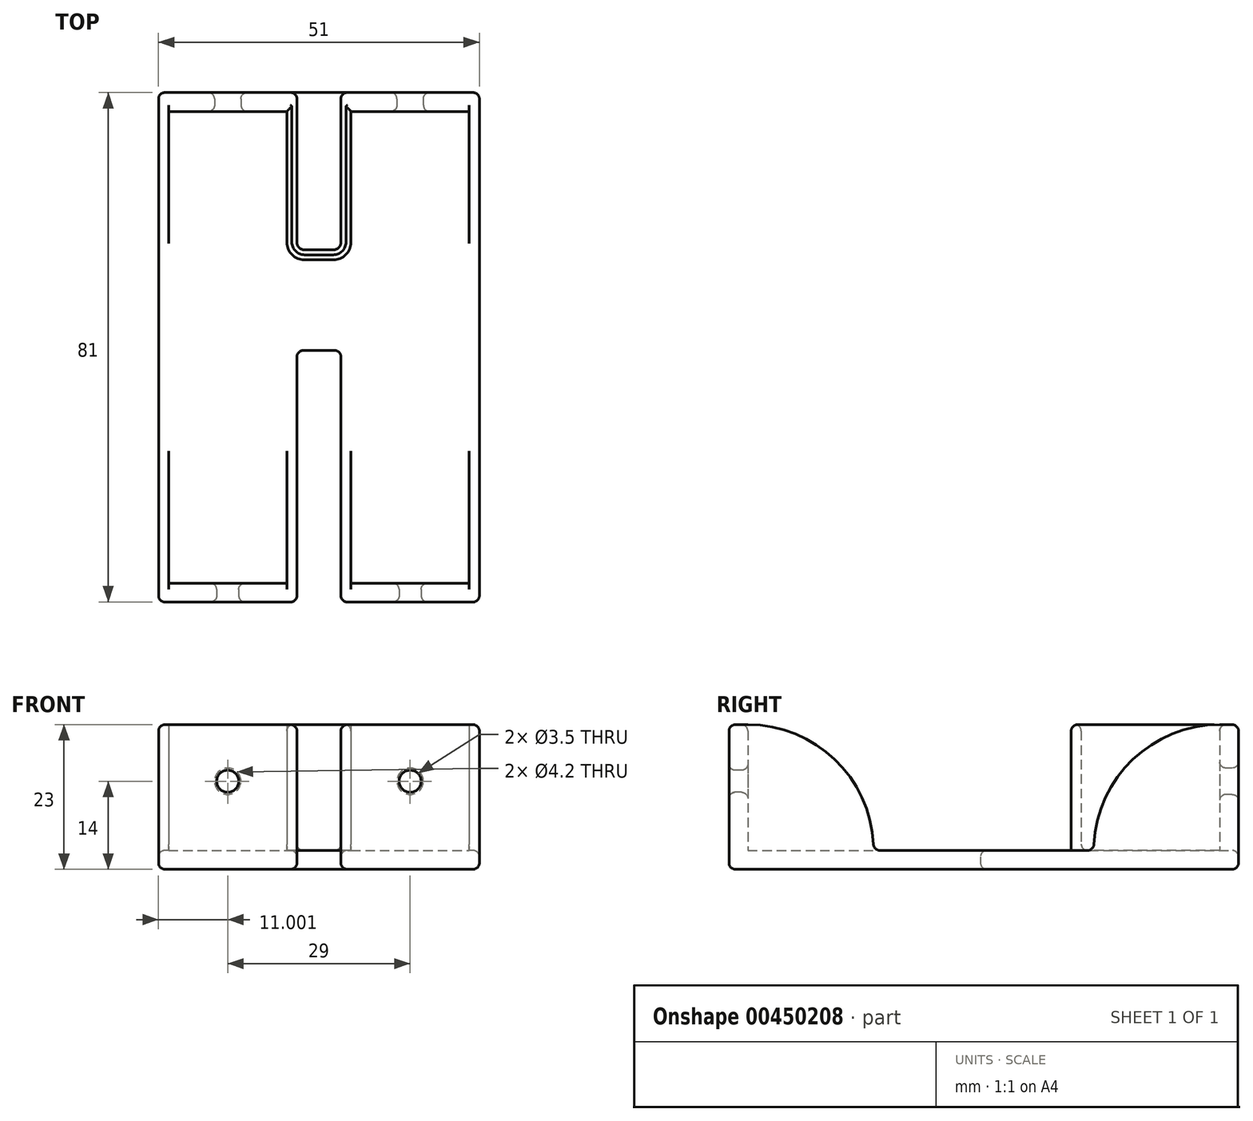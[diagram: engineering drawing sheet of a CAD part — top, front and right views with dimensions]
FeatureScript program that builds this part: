
annotation { "Feature Type Name" : "Feature", "Feature Type Description" : "" }
export const myFeature = defineFeature(function(context is Context, id is Id, definition is map)
    precondition{}
    {
        {
            var Q0;
            Q0=qCreatedBy(makeId("Top.planeOp"),FACE);
            var sketch = newSketch(context, id + "F0", { "sketchPlane" : qUnion([Q0])});
            skLineSegment(sketch, "E0", {"start": v(0.78, 0) * mm, "end": v(22.78, 0) * mm});
            skLineSegment(sketch, "E1", {"start": v(0.78, 0) * mm, "end": v(0.78, 3) * mm});
            skLineSegment(sketch, "E2", {"start": v(0.78, 3) * mm, "end": v(0.78, 78) * mm});
            skLineSegment(sketch, "E3", {"start": v(0.78, 78) * mm, "end": v(0.78, 81) * mm});
            skLineSegment(sketch, "E4", {"start": v(0.78, 81) * mm, "end": v(22.78, 81) * mm});
            skLineSegment(sketch, "E5", {"start": v(22.78, 81) * mm, "end": v(29.78, 81) * mm});
            skLineSegment(sketch, "E6", {"start": v(29.78, 81) * mm, "end": v(51.78, 81) * mm});
            skLineSegment(sketch, "E7", {"start": v(51.78, 81) * mm, "end": v(51.78, 0) * mm});
            skLineSegment(sketch, "E8", {"start": v(51.78, 0) * mm, "end": v(29.78, 0) * mm});
            skLineSegment(sketch, "E9", {"start": v(29.78, 0) * mm, "end": v(29.78, 40) * mm});
            skLineSegment(sketch, "E10", {"start": v(22.78, 0) * mm, "end": v(22.78, 40) * mm});
            skLineSegment(sketch, "E11", {"start": v(22.78, 40) * mm, "end": v(29.78, 40) * mm});
            skLineSegment(sketch, "E12", {"start": v(2.38, 78) * mm, "end": v(21.18, 78) * mm});
            skLineSegment(sketch, "E13", {"start": v(22.78, 78) * mm, "end": v(22.78, 81) * mm});
            skLineSegment(sketch, "E14", {"start": v(29.78, 81) * mm, "end": v(29.78, 78) * mm});
            skLineSegment(sketch, "E15", {"start": v(31.38, 78) * mm, "end": v(50.18, 78) * mm});
            skLineSegment(sketch, "E16", {"start": v(31.38, 3) * mm, "end": v(50.18, 3) * mm});
            skLineSegment(sketch, "E17", {"start": v(22.78, 78) * mm, "end": v(22.78, 57.2) * mm});
            skLineSegment(sketch, "E18", {"start": v(23.98, 56) * mm, "end": v(28.58, 56) * mm});
            skLineSegment(sketch, "E19", {"start": v(29.78, 57.2) * mm, "end": v(29.78, 78) * mm});
            skLineSegment(sketch, "E20.0", {"start": v(21.18, 78) * mm, "end": v(21.18, 57.2) * mm});
            skLineSegment(sketch, "E21.0", {"start": v(23.98, 54.4) * mm, "end": v(28.58, 54.4) * mm});
            skLineSegment(sketch, "E22.0", {"start": v(31.38, 57.2) * mm, "end": v(31.38, 78) * mm});
            skLineSegment(sketch, "E23", {"start": v(2.38, 78) * mm, "end": v(2.38, 58) * mm});
            skLineSegment(sketch, "E24", {"start": v(2.38, 58) * mm, "end": v(0.78, 58) * mm});
            skLineSegment(sketch, "E25", {"start": v(50.18, 78) * mm, "end": v(50.18, 58) * mm});
            skLineSegment(sketch, "E26", {"start": v(50.18, 58) * mm, "end": v(51.78, 58) * mm});
            skLineSegment(sketch, "E27", {"start": v(2.38, 3) * mm, "end": v(2.38, 23) * mm});
            skLineSegment(sketch, "E28", {"start": v(2.38, 23) * mm, "end": v(0.78, 23) * mm});
            skLineSegment(sketch, "E29", {"start": v(21.18, 3) * mm, "end": v(21.18, 23) * mm});
            skLineSegment(sketch, "E30", {"start": v(21.18, 23) * mm, "end": v(22.78, 23) * mm});
            skLineSegment(sketch, "E31", {"start": v(31.38, 3) * mm, "end": v(31.38, 23) * mm});
            skLineSegment(sketch, "E32", {"start": v(31.38, 23) * mm, "end": v(29.78, 23) * mm});
            skLineSegment(sketch, "E33", {"start": v(50.18, 3) * mm, "end": v(50.18, 23) * mm});
            skLineSegment(sketch, "E34", {"start": v(50.18, 23) * mm, "end": v(51.78, 23) * mm});
            skPoint(sketch, "E35.start.orphan", {"position": v(51.78, 3) * mm});
            skPoint(sketch, "E36.orphan", {"position": v(29.78, 3) * mm});
            skPoint(sketch, "E37.orphan", {"position": v(22.78, 3) * mm});
            skPoint(sketch, "E38.orphan", {"position": v(51.78, 78) * mm});
            skPoint(sketch, "E39.visualSharp", {"position": v(22.78, 56) * mm});
            skArc(sketch, "E39.filletArc", {"start": v(22.78, 57.2) * mm, "mid": v(23.13, 56.35) * mm, "end": v(23.98, 56) * mm});
            skPoint(sketch, "E40.visualSharp", {"position": v(29.78, 56) * mm});
            skArc(sketch, "E40.filletArc", {"start": v(28.58, 56) * mm, "mid": v(29.43, 56.35) * mm, "end": v(29.78, 57.2) * mm});
            skArc(sketch, "E41", {"start": v(23.98, 54.4) * mm, "mid": v(22, 55.22) * mm, "end": v(21.18, 57.2) * mm});
            skArc(sketch, "E42", {"start": v(28.58, 54.4) * mm, "mid": v(30.56, 55.22) * mm, "end": v(31.38, 57.2) * mm});
            skLineSegment(sketch, "E43", {"start": v(2.38, 3) * mm, "end": v(21.18, 3) * mm});
            skSolve(sketch);
        }
        {
            var Q0;
            {var subQ2=sQuery(id+"F0.wireOp",EDGE,"E3");Q0=makeQuery(id+"F0.imprint","IMPRINT",FACE,{"disambiguationData":[TD([[makeQuery(id+"F0.imprint","IMPRINT",EDGE,{"derivedFrom":subQ2}),-1.0]])]});}
            var Q1;
            {var subQ4=sQuery(id+"F0.wireOp",EDGE,"E0");Q1=makeQuery(id+"F0.imprint","IMPRINT",FACE,{"disambiguationData":[TD([[makeQuery(id+"F0.imprint","IMPRINT",EDGE,{"derivedFrom":subQ4}),1.0]])]});}
            var Q2;
            {var subQ1=sQuery(id+"F0.wireOp",EDGE,"E8");Q2=makeQuery(id+"F0.imprint","IMPRINT",FACE,{"disambiguationData":[TD([[makeQuery(id+"F0.imprint","IMPRINT",EDGE,{"derivedFrom":subQ1}),-1.0]])]});}
            extrude(context, id + "F1", {"entities" : qUnion([Q0, Q1, Q2]), "depth" : 23 * mm});
        }
        {
            var Q0;
            {var subQ5=sQuery(id+"F0.wireOp",EDGE,"E11");Q0=makeQuery(id+"F0.imprint","IMPRINT",FACE,{"disambiguationData":[TD([[makeQuery(id+"F0.imprint","IMPRINT",EDGE,{"derivedFrom":subQ5}),1.0]])]});}
            var Q1;
            Q1=makeQuery(id+"F0.imprint","IMPRINT",FACE,{"disambiguationData":[TD([[makeQuery(id+"F0.imprint","IMPRINT",EDGE,{"derivedFrom":sQuery(id+"F0.wireOp",EDGE,"E5")}),-1.0]])]});
            extrude(context, id + "F2", {"entities" : qUnion([Q0, Q1]), "operationType" : NewBodyOperationType.ADD, "depth" : 3 * mm});
        }
        {
            var Q0;
            Q0=makeQuery(id+"F1.opExtrude","CAP_EDGE",EDGE,{"disambiguationData":[OSD([sQuery(id+"F0.wireOp",EDGE,"E24")])],"isStart":false});
            var Q1;
            Q1=makeQuery(id+"F1.opExtrude","CAP_EDGE",EDGE,{"disambiguationData":[OSD([sQuery(id+"F0.wireOp",EDGE,"E26")])],"isStart":false});
            var Q2;
            Q2=makeQuery(id+"F1.opExtrude","CAP_EDGE",EDGE,{"disambiguationData":[OSD([sQuery(id+"F0.wireOp",EDGE,"E34")])],"isStart":false});
            var Q3;
            Q3=makeQuery(id+"F1.opExtrude","CAP_EDGE",EDGE,{"disambiguationData":[OSD([sQuery(id+"F0.wireOp",EDGE,"E32")])],"isStart":false});
            var Q4;
            Q4=makeQuery(id+"F1.opExtrude","CAP_EDGE",EDGE,{"disambiguationData":[OSD([sQuery(id+"F0.wireOp",EDGE,"E30")])],"isStart":false});
            var Q5;
            Q5=makeQuery(id+"F1.opExtrude","CAP_EDGE",EDGE,{"disambiguationData":[OSD([sQuery(id+"F0.wireOp",EDGE,"E28")])],"isStart":false});
            fillet(context, id + "F3", {"entities" : qUnion([Q0, Q1, Q2, Q3, Q4, Q5]), "radius" : 20 * mm, "tangentPropagation" : true, "allowEdgeOverflow" : false});
        }
        {
            var Q0;
            Q0=makeQuery(id+"F1.opExtrude","SWEPT_FACE",FACE,{"disambiguationData":[OSD([sQuery(id+"F0.wireOp",EDGE,"E0")])]});
            var sketch = newSketch(context, id + "F4", { "sketchPlane" : qUnion([Q0])});
            skCircle(sketch, "E44", {"center": v(11.78, 14) * mm, "radius": 1.75 * mm});
            skLineSegment(sketch, "E45.0.0", {"start": v(0.78, 0) * mm, "end": v(22.78, 0) * mm});
            skLineSegment(sketch, "E45.0.1", {"start": v(22.78, 0) * mm, "end": v(22.78, 23) * mm});
            skLineSegment(sketch, "E45.0.2", {"start": v(22.78, 23) * mm, "end": v(0.78, 23) * mm});
            skLineSegment(sketch, "E45.0.3", {"start": v(0.78, 23) * mm, "end": v(0.78, 0) * mm});
            skSolve(sketch);
        }
        {
            var Q0;
            Q0=makeQuery(id+"F1.opExtrude","SWEPT_FACE",FACE,{"disambiguationData":[OSD([sQuery(id+"F0.wireOp",EDGE,"E8")])]});
            var sketch = newSketch(context, id + "F5", { "sketchPlane" : qUnion([Q0])});
            skCircle(sketch, "E46", {"center": v(40.78, 14) * mm, "radius": 1.75 * mm});
            skSolve(sketch);
        }
        {
            var Q0;
            Q0=makeQuery(id+"F2.boolean.opBoolean","MERGE",FACE,{"derivedFrom":[makeQuery(id+"F1.opExtrude","SWEPT_FACE",FACE,{"disambiguationData":[OSD([sQuery(id+"F0.wireOp",EDGE,"E4")])]}),makeQuery(id+"F1.opExtrude","SWEPT_FACE",FACE,{"disambiguationData":[OSD([sQuery(id+"F0.wireOp",EDGE,"E6")])]}),makeQuery(id+"F2.opExtrude","SWEPT_FACE",FACE,{"disambiguationData":[OSD([sQuery(id+"F0.wireOp",EDGE,"E5")])]})]});
            var sketch = newSketch(context, id + "F6", { "sketchPlane" : qUnion([Q0])});
            skCircle(sketch, "E47", {"center": v(-40.78, 14) * mm, "radius": 2.1 * mm});
            skCircle(sketch, "E48", {"center": v(-11.78, 14) * mm, "radius": 2.1 * mm});
            skLineSegment(sketch, "E49.0.0", {"start": v(-51.78, 0) * mm, "end": v(-0.78, 0) * mm});
            skLineSegment(sketch, "E49.0.1", {"start": v(-0.78, 0) * mm, "end": v(-0.78, 23) * mm});
            skLineSegment(sketch, "E49.0.2", {"start": v(-0.78, 23) * mm, "end": v(-22.78, 23) * mm});
            skLineSegment(sketch, "E49.0.3", {"start": v(-22.78, 23) * mm, "end": v(-22.78, 3) * mm});
            skLineSegment(sketch, "E49.0.4", {"start": v(-22.78, 3) * mm, "end": v(-29.78, 3) * mm});
            skLineSegment(sketch, "E49.0.5", {"start": v(-29.78, 3) * mm, "end": v(-29.78, 23) * mm});
            skLineSegment(sketch, "E49.0.6", {"start": v(-29.78, 23) * mm, "end": v(-51.78, 23) * mm});
            skLineSegment(sketch, "E49.0.7", {"start": v(-51.78, 23) * mm, "end": v(-51.78, 0) * mm});
            skSolve(sketch);
        }
        {
            var Q0;
            Q0=makeQuery(id+"F6.imprint","IMPRINT",FACE,{"disambiguationData":[TD([[makeQuery(id+"F6.imprint","IMPRINT",EDGE,{"derivedFrom":sQuery(id+"F6.wireOp",EDGE,"E47")}),1.0]])]});
            var Q1;
            Q1=makeQuery(id+"F6.imprint","IMPRINT",FACE,{"disambiguationData":[TD([[makeQuery(id+"F6.imprint","IMPRINT",EDGE,{"derivedFrom":sQuery(id+"F6.wireOp",EDGE,"E48")}),1.0]])]});
            var Q2;
            Q2=makeQuery(id+"F5.imprint","IMPRINT",FACE,{"disambiguationData":[TD([[makeQuery(id+"F5.imprint","IMPRINT",EDGE,{"derivedFrom":sQuery(id+"F5.wireOp",EDGE,"E46")}),1.0]])]});
            var Q3;
            Q3=makeQuery(id+"F4.imprint","IMPRINT",FACE,{"disambiguationData":[TD([[makeQuery(id+"F4.imprint","IMPRINT",EDGE,{"derivedFrom":sQuery(id+"F4.wireOp",EDGE,"E44")}),1.0]])]});
            extrude(context, id + "F7", {"entities" : qUnion([Q0, Q1, Q2, Q3]), "operationType" : NewBodyOperationType.REMOVE, "endBound" : BoundingType.SYMMETRIC, "depth" : 25 * mm});
        }
        {
            var Q0;
            Q0=makeQuery(id+"F1.opExtrude","CAP_FACE",FACE,{"disambiguationData":[OSD([sQuery(id+"F0.wireOp",EDGE,"E2"),sQuery(id+"F0.wireOp",EDGE,"E3"),sQuery(id+"F0.wireOp",EDGE,"E4"),sQuery(id+"F0.wireOp",EDGE,"E6"),sQuery(id+"F0.wireOp",EDGE,"E7"),sQuery(id+"F0.wireOp",EDGE,"E12"),sQuery(id+"F0.wireOp",EDGE,"E13"),sQuery(id+"F0.wireOp",EDGE,"E14"),sQuery(id+"F0.wireOp",EDGE,"E15"),sQuery(id+"F0.wireOp",EDGE,"E17"),sQuery(id+"F0.wireOp",EDGE,"E18"),sQuery(id+"F0.wireOp",EDGE,"E19"),sQuery(id+"F0.wireOp",EDGE,"E20.0"),sQuery(id+"F0.wireOp",EDGE,"E21.0"),sQuery(id+"F0.wireOp",EDGE,"E22.0"),sQuery(id+"F0.wireOp",EDGE,"E23"),sQuery(id+"F0.wireOp",EDGE,"E24"),sQuery(id+"F0.wireOp",EDGE,"E25"),sQuery(id+"F0.wireOp",EDGE,"E26"),sQuery(id+"F0.wireOp",EDGE,"E39.filletArc"),sQuery(id+"F0.wireOp",EDGE,"E40.filletArc"),sQuery(id+"F0.wireOp",EDGE,"E41"),sQuery(id+"F0.wireOp",EDGE,"E42")])],"isStart":false});
            var Q1;
            Q1=makeQuery(id+"F1.opExtrude","CAP_FACE",FACE,{"disambiguationData":[OSD([sQuery(id+"F0.wireOp",EDGE,"E0"),sQuery(id+"F0.wireOp",EDGE,"E1"),sQuery(id+"F0.wireOp",EDGE,"E2"),sQuery(id+"F0.wireOp",EDGE,"E10"),sQuery(id+"F0.wireOp",EDGE,"E27"),sQuery(id+"F0.wireOp",EDGE,"E28"),sQuery(id+"F0.wireOp",EDGE,"E29"),sQuery(id+"F0.wireOp",EDGE,"E30"),sQuery(id+"F0.wireOp",EDGE,"E43")])],"isStart":false});
            var Q2;
            Q2=makeQuery(id+"F1.opExtrude","CAP_FACE",FACE,{"disambiguationData":[OSD([sQuery(id+"F0.wireOp",EDGE,"E7"),sQuery(id+"F0.wireOp",EDGE,"E8"),sQuery(id+"F0.wireOp",EDGE,"E9"),sQuery(id+"F0.wireOp",EDGE,"E16"),sQuery(id+"F0.wireOp",EDGE,"E31"),sQuery(id+"F0.wireOp",EDGE,"E32"),sQuery(id+"F0.wireOp",EDGE,"E33"),sQuery(id+"F0.wireOp",EDGE,"E34")])],"isStart":false});
            var Q3;
            Q3=makeQuery(id+"F2.opExtrude","CAP_EDGE",EDGE,{"disambiguationData":[OSD([sQuery(id+"F0.wireOp",EDGE,"E10")])],"isStart":false});
            var Q4;
            Q4=makeQuery(id+"F2.opExtrude","CAP_EDGE",EDGE,{"disambiguationData":[OSD([sQuery(id+"F0.wireOp",EDGE,"E9")])],"isStart":false});
            var Q5;
            Q5=makeQuery(id+"F2.opExtrude","CAP_EDGE",EDGE,{"disambiguationData":[OSD([sQuery(id+"F0.wireOp",EDGE,"E11")])],"isStart":false});
            var Q6;
            Q6=makeQuery(id+"F2.opExtrude","CAP_EDGE",EDGE,{"disambiguationData":[OSD([sQuery(id+"F0.wireOp",EDGE,"E7")])],"isStart":false});
            var Q7;
            Q7=makeQuery(id+"F2.opExtrude","CAP_EDGE",EDGE,{"disambiguationData":[OSD([sQuery(id+"F0.wireOp",EDGE,"E2")])],"isStart":false});
            var Q8;
            {var subQ0=sQuery(id+"F0.wireOp",EDGE,"E2");Q8=makeQuery(id+"F2.boolean.opBoolean","MERGE",FACE,{"derivedFrom":[makeQuery(id+"F1.opExtrude","SWEPT_FACE",FACE,{"disambiguationData":[OSD([sQuery(id+"F0.wireOp",EDGE,"E1"),subQ0])]}),makeQuery(id+"F1.opExtrude","SWEPT_FACE",FACE,{"disambiguationData":[OSD([subQ0,sQuery(id+"F0.wireOp",EDGE,"E3")])]}),makeQuery(id+"F2.opExtrude","SWEPT_FACE",FACE,{"disambiguationData":[OSD([subQ0])]})]});}
            var Q9;
            Q9=makeQuery(id+"F2.boolean.opBoolean","MERGE",FACE,{"derivedFrom":[makeQuery(id+"F1.opExtrude","SWEPT_FACE",FACE,{"disambiguationData":[OSD([sQuery(id+"F0.wireOp",EDGE,"E4")])]}),makeQuery(id+"F1.opExtrude","SWEPT_FACE",FACE,{"disambiguationData":[OSD([sQuery(id+"F0.wireOp",EDGE,"E6")])]}),makeQuery(id+"F2.opExtrude","SWEPT_FACE",FACE,{"disambiguationData":[OSD([sQuery(id+"F0.wireOp",EDGE,"E5")])]})]});
            var Q10;
            Q10=makeQuery(id+"F7.boolean.opBoolean","INTERSECT",EDGE,{"derivedFrom":[makeQuery(id+"F1.opExtrude","SWEPT_FACE",FACE,{"disambiguationData":[OSD([sQuery(id+"F0.wireOp",EDGE,"E12")])]}),makeQuery(id+"F7.opExtrude","SWEPT_FACE",FACE,{"disambiguationData":[OSD([sQuery(id+"F6.wireOp",EDGE,"E48")])]})]});
            var Q11;
            Q11=makeQuery(id+"F7.boolean.opBoolean","INTERSECT",EDGE,{"derivedFrom":[makeQuery(id+"F1.opExtrude","SWEPT_FACE",FACE,{"disambiguationData":[OSD([sQuery(id+"F0.wireOp",EDGE,"E15")])]}),makeQuery(id+"F7.opExtrude","SWEPT_FACE",FACE,{"disambiguationData":[OSD([sQuery(id+"F6.wireOp",EDGE,"E47")])]})]});
            var Q12;
            Q12=makeQuery(id+"F1.opExtrude","SWEPT_FACE",FACE,{"disambiguationData":[OSD([sQuery(id+"F0.wireOp",EDGE,"E8")])]});
            var Q13;
            Q13=makeQuery(id+"F1.opExtrude","SWEPT_FACE",FACE,{"disambiguationData":[OSD([sQuery(id+"F0.wireOp",EDGE,"E0")])]});
            var Q14;
            Q14=makeQuery(id+"F7.boolean.opBoolean","INTERSECT",EDGE,{"derivedFrom":[makeQuery(id+"F1.opExtrude","SWEPT_FACE",FACE,{"disambiguationData":[OSD([sQuery(id+"F0.wireOp",EDGE,"E43")])]}),makeQuery(id+"F7.opExtrude","SWEPT_FACE",FACE,{"disambiguationData":[OSD([sQuery(id+"F4.wireOp",EDGE,"E44")])]})]});
            var Q15;
            Q15=makeQuery(id+"F7.boolean.opBoolean","INTERSECT",EDGE,{"derivedFrom":[makeQuery(id+"F1.opExtrude","SWEPT_FACE",FACE,{"disambiguationData":[OSD([sQuery(id+"F0.wireOp",EDGE,"E16")])]}),makeQuery(id+"F7.opExtrude","SWEPT_FACE",FACE,{"disambiguationData":[OSD([sQuery(id+"F5.wireOp",EDGE,"E46")])]})]});
            var Q16;
            {var subQ0=sQuery(id+"F0.wireOp",EDGE,"E40.filletArc");var subQ1=sQuery(id+"F0.wireOp",EDGE,"E39.filletArc");var subQ2=sQuery(id+"F0.wireOp",EDGE,"E19");var subQ3=sQuery(id+"F0.wireOp",EDGE,"E18");var subQ4=sQuery(id+"F0.wireOp",EDGE,"E17");var subQ5=sQuery(id+"F0.wireOp",EDGE,"E14");var subQ6=sQuery(id+"F0.wireOp",EDGE,"E13");var subQ7=sQuery(id+"F0.wireOp",EDGE,"E43");var subQ8=sQuery(id+"F0.wireOp",EDGE,"E42");var subQ9=sQuery(id+"F0.wireOp",EDGE,"E41");var subQ10=sQuery(id+"F0.wireOp",EDGE,"E34");var subQ11=sQuery(id+"F0.wireOp",EDGE,"E33");var subQ12=sQuery(id+"F0.wireOp",EDGE,"E32");var subQ13=sQuery(id+"F0.wireOp",EDGE,"E31");var subQ14=sQuery(id+"F0.wireOp",EDGE,"E30");var subQ15=sQuery(id+"F0.wireOp",EDGE,"E29");var subQ16=sQuery(id+"F0.wireOp",EDGE,"E28");var subQ17=sQuery(id+"F0.wireOp",EDGE,"E27");var subQ18=sQuery(id+"F0.wireOp",EDGE,"E26");var subQ19=sQuery(id+"F0.wireOp",EDGE,"E25");var subQ20=sQuery(id+"F0.wireOp",EDGE,"E24");var subQ21=sQuery(id+"F0.wireOp",EDGE,"E23");var subQ22=sQuery(id+"F0.wireOp",EDGE,"E22.0");var subQ23=sQuery(id+"F0.wireOp",EDGE,"E21.0");var subQ24=sQuery(id+"F0.wireOp",EDGE,"E20.0");var subQ25=sQuery(id+"F0.wireOp",EDGE,"E16");var subQ26=sQuery(id+"F0.wireOp",EDGE,"E15");var subQ27=sQuery(id+"F0.wireOp",EDGE,"E12");var subQ28=sQuery(id+"F0.wireOp",EDGE,"E10");var subQ29=sQuery(id+"F0.wireOp",EDGE,"E9");var subQ30=sQuery(id+"F0.wireOp",EDGE,"E7");var subQ31=sQuery(id+"F0.wireOp",EDGE,"E2");Q16=makeQuery(id+"F2.boolean.opBoolean","MERGE",FACE,{"derivedFrom":[makeQuery(id+"F1.opExtrude","CAP_FACE",FACE,{"disambiguationData":[OSD([sQuery(id+"F0.wireOp",EDGE,"E0"),sQuery(id+"F0.wireOp",EDGE,"E1"),subQ31,subQ28,subQ17,subQ16,subQ15,subQ14,subQ7])],"isStart":true}),makeQuery(id+"F1.opExtrude","CAP_FACE",FACE,{"disambiguationData":[OSD([subQ31,sQuery(id+"F0.wireOp",EDGE,"E3"),sQuery(id+"F0.wireOp",EDGE,"E4"),sQuery(id+"F0.wireOp",EDGE,"E6"),subQ30,subQ27,subQ6,subQ5,subQ26,subQ4,subQ3,subQ2,subQ24,subQ23,subQ22,subQ21,subQ20,subQ19,subQ18,subQ1,subQ0,subQ9,subQ8])],"isStart":true}),makeQuery(id+"F1.opExtrude","CAP_FACE",FACE,{"disambiguationData":[OSD([subQ30,sQuery(id+"F0.wireOp",EDGE,"E8"),subQ29,subQ25,subQ13,subQ12,subQ11,subQ10])],"isStart":true}),makeQuery(id+"F2.opExtrude","CAP_FACE",FACE,{"disambiguationData":[OSD([subQ31,subQ30,subQ29,subQ28,sQuery(id+"F0.wireOp",EDGE,"E11"),subQ27,subQ26,subQ25,subQ24,subQ23,subQ22,subQ21,subQ20,subQ19,subQ18,subQ17,subQ16,subQ15,subQ14,subQ13,subQ12,subQ11,subQ10,subQ9,subQ8,subQ7])],"isStart":true}),makeQuery(id+"F2.opExtrude","CAP_FACE",FACE,{"disambiguationData":[OSD([sQuery(id+"F0.wireOp",EDGE,"E5"),subQ6,subQ5,subQ4,subQ3,subQ2,subQ1,subQ0])],"isStart":true})]});}
            var Q17;
            Q17=makeQuery(id+"F2.opExtrude","CAP_EDGE",EDGE,{"disambiguationData":[OSD([sQuery(id+"F0.wireOp",EDGE,"E21.0")])],"isStart":false});
            var Q18;
            Q18=makeQuery(id+"F2.opExtrude","CAP_EDGE",EDGE,{"disambiguationData":[OSD([sQuery(id+"F0.wireOp",EDGE,"E42")])],"isStart":false});
            var Q19;
            Q19=makeQuery(id+"F2.opExtrude","CAP_EDGE",EDGE,{"disambiguationData":[OSD([sQuery(id+"F0.wireOp",EDGE,"E23")])],"isStart":false});
            var Q20;
            Q20=makeQuery(id+"F2.opExtrude","CAP_EDGE",EDGE,{"disambiguationData":[OSD([sQuery(id+"F0.wireOp",EDGE,"E12")])],"isStart":false});
            var Q21;
            {var subQ0=sQuery(id+"F0.wireOp",EDGE,"E24");Q21=makeQuery(id+"F3.opFillet","BLEND_EDGE",EDGE,{"blendedFrom":[makeQuery(id+"F1.opExtrude","CAP_EDGE",EDGE,{"disambiguationData":[OSD([subQ0])],"isStart":false}),makeQuery(id+"F2.opExtrude","CAP_FACE",FACE,{"disambiguationData":[OSD([sQuery(id+"F0.wireOp",EDGE,"E2"),sQuery(id+"F0.wireOp",EDGE,"E7"),sQuery(id+"F0.wireOp",EDGE,"E9"),sQuery(id+"F0.wireOp",EDGE,"E10"),sQuery(id+"F0.wireOp",EDGE,"E11"),sQuery(id+"F0.wireOp",EDGE,"E12"),sQuery(id+"F0.wireOp",EDGE,"E15"),sQuery(id+"F0.wireOp",EDGE,"E16"),sQuery(id+"F0.wireOp",EDGE,"E20.0"),sQuery(id+"F0.wireOp",EDGE,"E21.0"),sQuery(id+"F0.wireOp",EDGE,"E22.0"),sQuery(id+"F0.wireOp",EDGE,"E23"),subQ0,sQuery(id+"F0.wireOp",EDGE,"E25"),sQuery(id+"F0.wireOp",EDGE,"E26"),sQuery(id+"F0.wireOp",EDGE,"E27"),sQuery(id+"F0.wireOp",EDGE,"E28"),sQuery(id+"F0.wireOp",EDGE,"E29"),sQuery(id+"F0.wireOp",EDGE,"E30"),sQuery(id+"F0.wireOp",EDGE,"E31"),sQuery(id+"F0.wireOp",EDGE,"E32"),sQuery(id+"F0.wireOp",EDGE,"E33"),sQuery(id+"F0.wireOp",EDGE,"E34"),sQuery(id+"F0.wireOp",EDGE,"E41"),sQuery(id+"F0.wireOp",EDGE,"E42"),sQuery(id+"F0.wireOp",EDGE,"E43")])],"isStart":false})],"blendedInto":[makeQuery(id+"F2.opExtrude","CAP_FACE",FACE,{"disambiguationData":[OSD([sQuery(id+"F0.wireOp",EDGE,"E2"),sQuery(id+"F0.wireOp",EDGE,"E7"),sQuery(id+"F0.wireOp",EDGE,"E9"),sQuery(id+"F0.wireOp",EDGE,"E10"),sQuery(id+"F0.wireOp",EDGE,"E11"),sQuery(id+"F0.wireOp",EDGE,"E12"),sQuery(id+"F0.wireOp",EDGE,"E15"),sQuery(id+"F0.wireOp",EDGE,"E16"),sQuery(id+"F0.wireOp",EDGE,"E20.0"),sQuery(id+"F0.wireOp",EDGE,"E21.0"),sQuery(id+"F0.wireOp",EDGE,"E22.0"),sQuery(id+"F0.wireOp",EDGE,"E23"),subQ0,sQuery(id+"F0.wireOp",EDGE,"E25"),sQuery(id+"F0.wireOp",EDGE,"E26"),sQuery(id+"F0.wireOp",EDGE,"E27"),sQuery(id+"F0.wireOp",EDGE,"E28"),sQuery(id+"F0.wireOp",EDGE,"E29"),sQuery(id+"F0.wireOp",EDGE,"E30"),sQuery(id+"F0.wireOp",EDGE,"E31"),sQuery(id+"F0.wireOp",EDGE,"E32"),sQuery(id+"F0.wireOp",EDGE,"E33"),sQuery(id+"F0.wireOp",EDGE,"E34"),sQuery(id+"F0.wireOp",EDGE,"E41"),sQuery(id+"F0.wireOp",EDGE,"E42"),sQuery(id+"F0.wireOp",EDGE,"E43")])],"isStart":false})]});}
            var Q22;
            Q22=makeQuery(id+"F2.opExtrude","CAP_EDGE",EDGE,{"disambiguationData":[OSD([sQuery(id+"F0.wireOp",EDGE,"E15")])],"isStart":false});
            var Q23;
            Q23=makeQuery(id+"F2.opExtrude","CAP_EDGE",EDGE,{"disambiguationData":[OSD([sQuery(id+"F0.wireOp",EDGE,"E25")])],"isStart":false});
            var Q24;
            {var subQ0=sQuery(id+"F0.wireOp",EDGE,"E26");Q24=makeQuery(id+"F3.opFillet","BLEND_EDGE",EDGE,{"blendedFrom":[makeQuery(id+"F1.opExtrude","CAP_EDGE",EDGE,{"disambiguationData":[OSD([subQ0])],"isStart":false}),makeQuery(id+"F2.opExtrude","CAP_FACE",FACE,{"disambiguationData":[OSD([sQuery(id+"F0.wireOp",EDGE,"E2"),sQuery(id+"F0.wireOp",EDGE,"E7"),sQuery(id+"F0.wireOp",EDGE,"E9"),sQuery(id+"F0.wireOp",EDGE,"E10"),sQuery(id+"F0.wireOp",EDGE,"E11"),sQuery(id+"F0.wireOp",EDGE,"E12"),sQuery(id+"F0.wireOp",EDGE,"E15"),sQuery(id+"F0.wireOp",EDGE,"E16"),sQuery(id+"F0.wireOp",EDGE,"E20.0"),sQuery(id+"F0.wireOp",EDGE,"E21.0"),sQuery(id+"F0.wireOp",EDGE,"E22.0"),sQuery(id+"F0.wireOp",EDGE,"E23"),sQuery(id+"F0.wireOp",EDGE,"E24"),sQuery(id+"F0.wireOp",EDGE,"E25"),subQ0,sQuery(id+"F0.wireOp",EDGE,"E27"),sQuery(id+"F0.wireOp",EDGE,"E28"),sQuery(id+"F0.wireOp",EDGE,"E29"),sQuery(id+"F0.wireOp",EDGE,"E30"),sQuery(id+"F0.wireOp",EDGE,"E31"),sQuery(id+"F0.wireOp",EDGE,"E32"),sQuery(id+"F0.wireOp",EDGE,"E33"),sQuery(id+"F0.wireOp",EDGE,"E34"),sQuery(id+"F0.wireOp",EDGE,"E41"),sQuery(id+"F0.wireOp",EDGE,"E42"),sQuery(id+"F0.wireOp",EDGE,"E43")])],"isStart":false})],"blendedInto":[makeQuery(id+"F2.opExtrude","CAP_FACE",FACE,{"disambiguationData":[OSD([sQuery(id+"F0.wireOp",EDGE,"E2"),sQuery(id+"F0.wireOp",EDGE,"E7"),sQuery(id+"F0.wireOp",EDGE,"E9"),sQuery(id+"F0.wireOp",EDGE,"E10"),sQuery(id+"F0.wireOp",EDGE,"E11"),sQuery(id+"F0.wireOp",EDGE,"E12"),sQuery(id+"F0.wireOp",EDGE,"E15"),sQuery(id+"F0.wireOp",EDGE,"E16"),sQuery(id+"F0.wireOp",EDGE,"E20.0"),sQuery(id+"F0.wireOp",EDGE,"E21.0"),sQuery(id+"F0.wireOp",EDGE,"E22.0"),sQuery(id+"F0.wireOp",EDGE,"E23"),sQuery(id+"F0.wireOp",EDGE,"E24"),sQuery(id+"F0.wireOp",EDGE,"E25"),subQ0,sQuery(id+"F0.wireOp",EDGE,"E27"),sQuery(id+"F0.wireOp",EDGE,"E28"),sQuery(id+"F0.wireOp",EDGE,"E29"),sQuery(id+"F0.wireOp",EDGE,"E30"),sQuery(id+"F0.wireOp",EDGE,"E31"),sQuery(id+"F0.wireOp",EDGE,"E32"),sQuery(id+"F0.wireOp",EDGE,"E33"),sQuery(id+"F0.wireOp",EDGE,"E34"),sQuery(id+"F0.wireOp",EDGE,"E41"),sQuery(id+"F0.wireOp",EDGE,"E42"),sQuery(id+"F0.wireOp",EDGE,"E43")])],"isStart":false})]});}
            var Q25;
            {var subQ0=sQuery(id+"F0.wireOp",EDGE,"E34");Q25=makeQuery(id+"F3.opFillet","BLEND_EDGE",EDGE,{"blendedFrom":[makeQuery(id+"F1.opExtrude","CAP_EDGE",EDGE,{"disambiguationData":[OSD([subQ0])],"isStart":false}),makeQuery(id+"F2.opExtrude","CAP_FACE",FACE,{"disambiguationData":[OSD([sQuery(id+"F0.wireOp",EDGE,"E2"),sQuery(id+"F0.wireOp",EDGE,"E7"),sQuery(id+"F0.wireOp",EDGE,"E9"),sQuery(id+"F0.wireOp",EDGE,"E10"),sQuery(id+"F0.wireOp",EDGE,"E11"),sQuery(id+"F0.wireOp",EDGE,"E12"),sQuery(id+"F0.wireOp",EDGE,"E15"),sQuery(id+"F0.wireOp",EDGE,"E16"),sQuery(id+"F0.wireOp",EDGE,"E20.0"),sQuery(id+"F0.wireOp",EDGE,"E21.0"),sQuery(id+"F0.wireOp",EDGE,"E22.0"),sQuery(id+"F0.wireOp",EDGE,"E23"),sQuery(id+"F0.wireOp",EDGE,"E24"),sQuery(id+"F0.wireOp",EDGE,"E25"),sQuery(id+"F0.wireOp",EDGE,"E26"),sQuery(id+"F0.wireOp",EDGE,"E27"),sQuery(id+"F0.wireOp",EDGE,"E28"),sQuery(id+"F0.wireOp",EDGE,"E29"),sQuery(id+"F0.wireOp",EDGE,"E30"),sQuery(id+"F0.wireOp",EDGE,"E31"),sQuery(id+"F0.wireOp",EDGE,"E32"),sQuery(id+"F0.wireOp",EDGE,"E33"),subQ0,sQuery(id+"F0.wireOp",EDGE,"E41"),sQuery(id+"F0.wireOp",EDGE,"E42"),sQuery(id+"F0.wireOp",EDGE,"E43")])],"isStart":false})],"blendedInto":[makeQuery(id+"F2.opExtrude","CAP_FACE",FACE,{"disambiguationData":[OSD([sQuery(id+"F0.wireOp",EDGE,"E2"),sQuery(id+"F0.wireOp",EDGE,"E7"),sQuery(id+"F0.wireOp",EDGE,"E9"),sQuery(id+"F0.wireOp",EDGE,"E10"),sQuery(id+"F0.wireOp",EDGE,"E11"),sQuery(id+"F0.wireOp",EDGE,"E12"),sQuery(id+"F0.wireOp",EDGE,"E15"),sQuery(id+"F0.wireOp",EDGE,"E16"),sQuery(id+"F0.wireOp",EDGE,"E20.0"),sQuery(id+"F0.wireOp",EDGE,"E21.0"),sQuery(id+"F0.wireOp",EDGE,"E22.0"),sQuery(id+"F0.wireOp",EDGE,"E23"),sQuery(id+"F0.wireOp",EDGE,"E24"),sQuery(id+"F0.wireOp",EDGE,"E25"),sQuery(id+"F0.wireOp",EDGE,"E26"),sQuery(id+"F0.wireOp",EDGE,"E27"),sQuery(id+"F0.wireOp",EDGE,"E28"),sQuery(id+"F0.wireOp",EDGE,"E29"),sQuery(id+"F0.wireOp",EDGE,"E30"),sQuery(id+"F0.wireOp",EDGE,"E31"),sQuery(id+"F0.wireOp",EDGE,"E32"),sQuery(id+"F0.wireOp",EDGE,"E33"),subQ0,sQuery(id+"F0.wireOp",EDGE,"E41"),sQuery(id+"F0.wireOp",EDGE,"E42"),sQuery(id+"F0.wireOp",EDGE,"E43")])],"isStart":false})]});}
            var Q26;
            {var subQ0=sQuery(id+"F0.wireOp",EDGE,"E32");Q26=makeQuery(id+"F3.opFillet","BLEND_EDGE",EDGE,{"blendedFrom":[makeQuery(id+"F1.opExtrude","CAP_EDGE",EDGE,{"disambiguationData":[OSD([subQ0])],"isStart":false}),makeQuery(id+"F2.opExtrude","CAP_FACE",FACE,{"disambiguationData":[OSD([sQuery(id+"F0.wireOp",EDGE,"E2"),sQuery(id+"F0.wireOp",EDGE,"E7"),sQuery(id+"F0.wireOp",EDGE,"E9"),sQuery(id+"F0.wireOp",EDGE,"E10"),sQuery(id+"F0.wireOp",EDGE,"E11"),sQuery(id+"F0.wireOp",EDGE,"E12"),sQuery(id+"F0.wireOp",EDGE,"E15"),sQuery(id+"F0.wireOp",EDGE,"E16"),sQuery(id+"F0.wireOp",EDGE,"E20.0"),sQuery(id+"F0.wireOp",EDGE,"E21.0"),sQuery(id+"F0.wireOp",EDGE,"E22.0"),sQuery(id+"F0.wireOp",EDGE,"E23"),sQuery(id+"F0.wireOp",EDGE,"E24"),sQuery(id+"F0.wireOp",EDGE,"E25"),sQuery(id+"F0.wireOp",EDGE,"E26"),sQuery(id+"F0.wireOp",EDGE,"E27"),sQuery(id+"F0.wireOp",EDGE,"E28"),sQuery(id+"F0.wireOp",EDGE,"E29"),sQuery(id+"F0.wireOp",EDGE,"E30"),sQuery(id+"F0.wireOp",EDGE,"E31"),subQ0,sQuery(id+"F0.wireOp",EDGE,"E33"),sQuery(id+"F0.wireOp",EDGE,"E34"),sQuery(id+"F0.wireOp",EDGE,"E41"),sQuery(id+"F0.wireOp",EDGE,"E42"),sQuery(id+"F0.wireOp",EDGE,"E43")])],"isStart":false})],"blendedInto":[makeQuery(id+"F2.opExtrude","CAP_FACE",FACE,{"disambiguationData":[OSD([sQuery(id+"F0.wireOp",EDGE,"E2"),sQuery(id+"F0.wireOp",EDGE,"E7"),sQuery(id+"F0.wireOp",EDGE,"E9"),sQuery(id+"F0.wireOp",EDGE,"E10"),sQuery(id+"F0.wireOp",EDGE,"E11"),sQuery(id+"F0.wireOp",EDGE,"E12"),sQuery(id+"F0.wireOp",EDGE,"E15"),sQuery(id+"F0.wireOp",EDGE,"E16"),sQuery(id+"F0.wireOp",EDGE,"E20.0"),sQuery(id+"F0.wireOp",EDGE,"E21.0"),sQuery(id+"F0.wireOp",EDGE,"E22.0"),sQuery(id+"F0.wireOp",EDGE,"E23"),sQuery(id+"F0.wireOp",EDGE,"E24"),sQuery(id+"F0.wireOp",EDGE,"E25"),sQuery(id+"F0.wireOp",EDGE,"E26"),sQuery(id+"F0.wireOp",EDGE,"E27"),sQuery(id+"F0.wireOp",EDGE,"E28"),sQuery(id+"F0.wireOp",EDGE,"E29"),sQuery(id+"F0.wireOp",EDGE,"E30"),sQuery(id+"F0.wireOp",EDGE,"E31"),subQ0,sQuery(id+"F0.wireOp",EDGE,"E33"),sQuery(id+"F0.wireOp",EDGE,"E34"),sQuery(id+"F0.wireOp",EDGE,"E41"),sQuery(id+"F0.wireOp",EDGE,"E42"),sQuery(id+"F0.wireOp",EDGE,"E43")])],"isStart":false})]});}
            var Q27;
            {var subQ0=sQuery(id+"F0.wireOp",EDGE,"E30");Q27=makeQuery(id+"F3.opFillet","BLEND_EDGE",EDGE,{"blendedFrom":[makeQuery(id+"F1.opExtrude","CAP_EDGE",EDGE,{"disambiguationData":[OSD([subQ0])],"isStart":false}),makeQuery(id+"F2.opExtrude","CAP_FACE",FACE,{"disambiguationData":[OSD([sQuery(id+"F0.wireOp",EDGE,"E2"),sQuery(id+"F0.wireOp",EDGE,"E7"),sQuery(id+"F0.wireOp",EDGE,"E9"),sQuery(id+"F0.wireOp",EDGE,"E10"),sQuery(id+"F0.wireOp",EDGE,"E11"),sQuery(id+"F0.wireOp",EDGE,"E12"),sQuery(id+"F0.wireOp",EDGE,"E15"),sQuery(id+"F0.wireOp",EDGE,"E16"),sQuery(id+"F0.wireOp",EDGE,"E20.0"),sQuery(id+"F0.wireOp",EDGE,"E21.0"),sQuery(id+"F0.wireOp",EDGE,"E22.0"),sQuery(id+"F0.wireOp",EDGE,"E23"),sQuery(id+"F0.wireOp",EDGE,"E24"),sQuery(id+"F0.wireOp",EDGE,"E25"),sQuery(id+"F0.wireOp",EDGE,"E26"),sQuery(id+"F0.wireOp",EDGE,"E27"),sQuery(id+"F0.wireOp",EDGE,"E28"),sQuery(id+"F0.wireOp",EDGE,"E29"),subQ0,sQuery(id+"F0.wireOp",EDGE,"E31"),sQuery(id+"F0.wireOp",EDGE,"E32"),sQuery(id+"F0.wireOp",EDGE,"E33"),sQuery(id+"F0.wireOp",EDGE,"E34"),sQuery(id+"F0.wireOp",EDGE,"E41"),sQuery(id+"F0.wireOp",EDGE,"E42"),sQuery(id+"F0.wireOp",EDGE,"E43")])],"isStart":false})],"blendedInto":[makeQuery(id+"F2.opExtrude","CAP_FACE",FACE,{"disambiguationData":[OSD([sQuery(id+"F0.wireOp",EDGE,"E2"),sQuery(id+"F0.wireOp",EDGE,"E7"),sQuery(id+"F0.wireOp",EDGE,"E9"),sQuery(id+"F0.wireOp",EDGE,"E10"),sQuery(id+"F0.wireOp",EDGE,"E11"),sQuery(id+"F0.wireOp",EDGE,"E12"),sQuery(id+"F0.wireOp",EDGE,"E15"),sQuery(id+"F0.wireOp",EDGE,"E16"),sQuery(id+"F0.wireOp",EDGE,"E20.0"),sQuery(id+"F0.wireOp",EDGE,"E21.0"),sQuery(id+"F0.wireOp",EDGE,"E22.0"),sQuery(id+"F0.wireOp",EDGE,"E23"),sQuery(id+"F0.wireOp",EDGE,"E24"),sQuery(id+"F0.wireOp",EDGE,"E25"),sQuery(id+"F0.wireOp",EDGE,"E26"),sQuery(id+"F0.wireOp",EDGE,"E27"),sQuery(id+"F0.wireOp",EDGE,"E28"),sQuery(id+"F0.wireOp",EDGE,"E29"),subQ0,sQuery(id+"F0.wireOp",EDGE,"E31"),sQuery(id+"F0.wireOp",EDGE,"E32"),sQuery(id+"F0.wireOp",EDGE,"E33"),sQuery(id+"F0.wireOp",EDGE,"E34"),sQuery(id+"F0.wireOp",EDGE,"E41"),sQuery(id+"F0.wireOp",EDGE,"E42"),sQuery(id+"F0.wireOp",EDGE,"E43")])],"isStart":false})]});}
            var Q28;
            {var subQ0=sQuery(id+"F0.wireOp",EDGE,"E28");Q28=makeQuery(id+"F3.opFillet","BLEND_EDGE",EDGE,{"blendedFrom":[makeQuery(id+"F1.opExtrude","CAP_EDGE",EDGE,{"disambiguationData":[OSD([subQ0])],"isStart":false}),makeQuery(id+"F2.opExtrude","CAP_FACE",FACE,{"disambiguationData":[OSD([sQuery(id+"F0.wireOp",EDGE,"E2"),sQuery(id+"F0.wireOp",EDGE,"E7"),sQuery(id+"F0.wireOp",EDGE,"E9"),sQuery(id+"F0.wireOp",EDGE,"E10"),sQuery(id+"F0.wireOp",EDGE,"E11"),sQuery(id+"F0.wireOp",EDGE,"E12"),sQuery(id+"F0.wireOp",EDGE,"E15"),sQuery(id+"F0.wireOp",EDGE,"E16"),sQuery(id+"F0.wireOp",EDGE,"E20.0"),sQuery(id+"F0.wireOp",EDGE,"E21.0"),sQuery(id+"F0.wireOp",EDGE,"E22.0"),sQuery(id+"F0.wireOp",EDGE,"E23"),sQuery(id+"F0.wireOp",EDGE,"E24"),sQuery(id+"F0.wireOp",EDGE,"E25"),sQuery(id+"F0.wireOp",EDGE,"E26"),sQuery(id+"F0.wireOp",EDGE,"E27"),subQ0,sQuery(id+"F0.wireOp",EDGE,"E29"),sQuery(id+"F0.wireOp",EDGE,"E30"),sQuery(id+"F0.wireOp",EDGE,"E31"),sQuery(id+"F0.wireOp",EDGE,"E32"),sQuery(id+"F0.wireOp",EDGE,"E33"),sQuery(id+"F0.wireOp",EDGE,"E34"),sQuery(id+"F0.wireOp",EDGE,"E41"),sQuery(id+"F0.wireOp",EDGE,"E42"),sQuery(id+"F0.wireOp",EDGE,"E43")])],"isStart":false})],"blendedInto":[makeQuery(id+"F2.opExtrude","CAP_FACE",FACE,{"disambiguationData":[OSD([sQuery(id+"F0.wireOp",EDGE,"E2"),sQuery(id+"F0.wireOp",EDGE,"E7"),sQuery(id+"F0.wireOp",EDGE,"E9"),sQuery(id+"F0.wireOp",EDGE,"E10"),sQuery(id+"F0.wireOp",EDGE,"E11"),sQuery(id+"F0.wireOp",EDGE,"E12"),sQuery(id+"F0.wireOp",EDGE,"E15"),sQuery(id+"F0.wireOp",EDGE,"E16"),sQuery(id+"F0.wireOp",EDGE,"E20.0"),sQuery(id+"F0.wireOp",EDGE,"E21.0"),sQuery(id+"F0.wireOp",EDGE,"E22.0"),sQuery(id+"F0.wireOp",EDGE,"E23"),sQuery(id+"F0.wireOp",EDGE,"E24"),sQuery(id+"F0.wireOp",EDGE,"E25"),sQuery(id+"F0.wireOp",EDGE,"E26"),sQuery(id+"F0.wireOp",EDGE,"E27"),subQ0,sQuery(id+"F0.wireOp",EDGE,"E29"),sQuery(id+"F0.wireOp",EDGE,"E30"),sQuery(id+"F0.wireOp",EDGE,"E31"),sQuery(id+"F0.wireOp",EDGE,"E32"),sQuery(id+"F0.wireOp",EDGE,"E33"),sQuery(id+"F0.wireOp",EDGE,"E34"),sQuery(id+"F0.wireOp",EDGE,"E41"),sQuery(id+"F0.wireOp",EDGE,"E42"),sQuery(id+"F0.wireOp",EDGE,"E43")])],"isStart":false})]});}
            var Q29;
            Q29=makeQuery(id+"F2.opExtrude","CAP_EDGE",EDGE,{"disambiguationData":[OSD([sQuery(id+"F0.wireOp",EDGE,"E27")])],"isStart":false});
            var Q30;
            Q30=makeQuery(id+"F2.opExtrude","CAP_EDGE",EDGE,{"disambiguationData":[OSD([sQuery(id+"F0.wireOp",EDGE,"E43")])],"isStart":false});
            var Q31;
            Q31=makeQuery(id+"F2.opExtrude","CAP_EDGE",EDGE,{"disambiguationData":[OSD([sQuery(id+"F0.wireOp",EDGE,"E29")])],"isStart":false});
            var Q32;
            Q32=makeQuery(id+"F2.opExtrude","CAP_EDGE",EDGE,{"disambiguationData":[OSD([sQuery(id+"F0.wireOp",EDGE,"E31")])],"isStart":false});
            var Q33;
            Q33=makeQuery(id+"F2.opExtrude","CAP_EDGE",EDGE,{"disambiguationData":[OSD([sQuery(id+"F0.wireOp",EDGE,"E33")])],"isStart":false});
            var Q34;
            Q34=makeQuery(id+"F2.opExtrude","CAP_EDGE",EDGE,{"disambiguationData":[OSD([sQuery(id+"F0.wireOp",EDGE,"E16")])],"isStart":false});
            var Q35;
            Q35=makeQuery(id+"F2.opExtrude","CAP_FACE",FACE,{"disambiguationData":[OSD([sQuery(id+"F0.wireOp",EDGE,"E5"),sQuery(id+"F0.wireOp",EDGE,"E13"),sQuery(id+"F0.wireOp",EDGE,"E14"),sQuery(id+"F0.wireOp",EDGE,"E17"),sQuery(id+"F0.wireOp",EDGE,"E18"),sQuery(id+"F0.wireOp",EDGE,"E19"),sQuery(id+"F0.wireOp",EDGE,"E39.filletArc"),sQuery(id+"F0.wireOp",EDGE,"E40.filletArc")])],"isStart":false});
            var Q36;
            Q36=makeQuery(id+"F7.boolean.opBoolean","COPY",FACE,{"derivedFrom":makeQuery(id+"F7.opExtrude","SWEPT_FACE",FACE,{"disambiguationData":[OSD([sQuery(id+"F6.wireOp",EDGE,"E47")])]})});
            var Q37;
            Q37=makeQuery(id+"F2.opExtrude","SWEPT_EDGE",EDGE,{"disambiguationData":[OSD([sQuery(id+"F0.wireOp",EDGE,"E10"),sQuery(id+"F0.wireOp",EDGE,"E11")])]});
            var Q38;
            Q38=makeQuery(id+"F2.opExtrude","SWEPT_EDGE",EDGE,{"disambiguationData":[OSD([sQuery(id+"F0.wireOp",EDGE,"E9"),sQuery(id+"F0.wireOp",EDGE,"E11")])]});
            fillet(context, id + "F8", {"entities" : qUnion([Q0, Q1, Q2, Q3, Q4, Q5, Q6, Q7, Q8, Q9, Q10, Q11, Q12, Q13, Q14, Q15, Q16, Q17, Q18, Q19, Q20, Q21, Q22, Q23, Q24, Q25, Q26, Q27, Q28, Q29, Q30, Q31, Q32, Q33, Q34, Q35, Q36, Q37, Q38]), "radius" : 1 * mm, "tangentPropagation" : true, "allowEdgeOverflow" : false});
        }
    });
